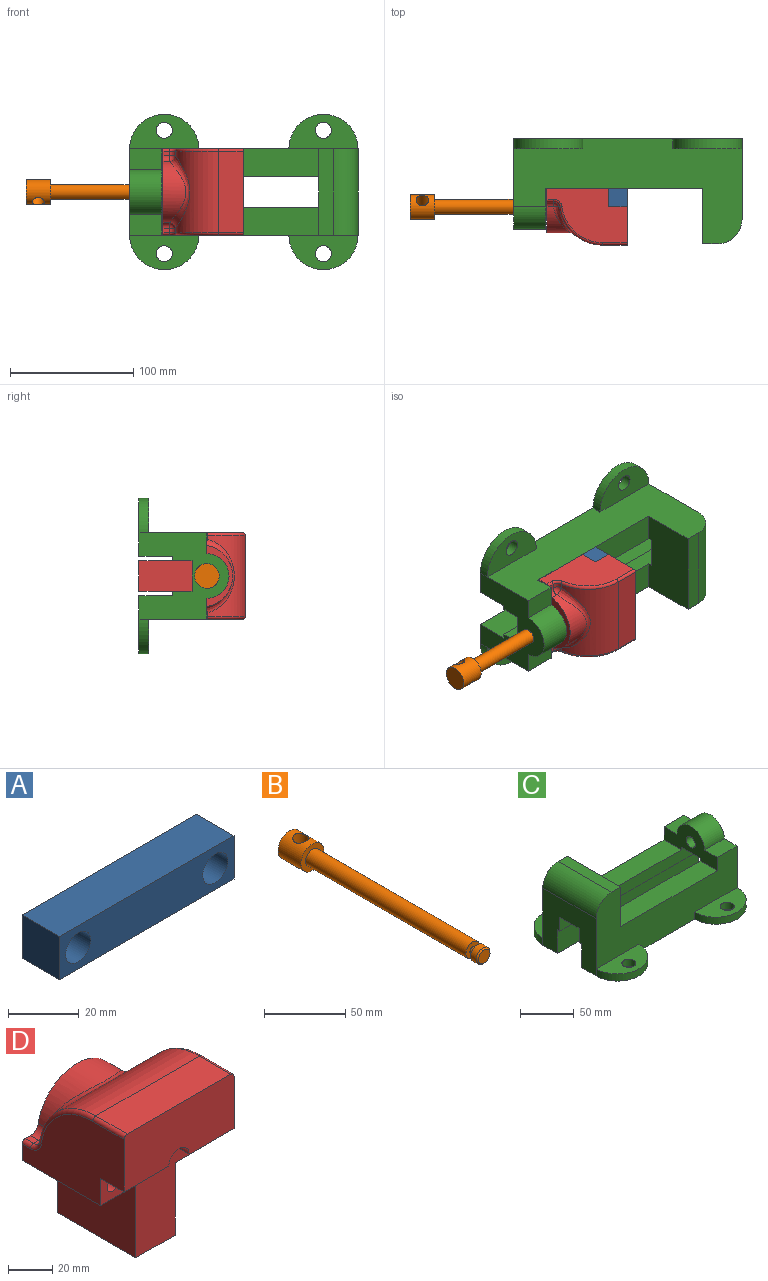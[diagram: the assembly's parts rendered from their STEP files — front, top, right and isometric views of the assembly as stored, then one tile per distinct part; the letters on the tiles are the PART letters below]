
ASSEMBLY  parts=4 mates=7
PART A: 16 faces, bbox 70x15x15 mm
  f0: plane 70x15mm, normal (0,1,0), area 958.9mm2, adj f1,f3,f4,f5,f6,f9,f12
  f1: plane 70x15mm, normal (0,0,1), area 1050mm2, adj f0,f2,f4,f5
  f2: plane 70x15mm, normal (0,-1,0), area 892.9mm2, adj f1,f3,f4,f5,f8,f11
  f3: plane 70x15mm, normal (0,0,-1), area 960mm2, adj f0,f2,f4,f5,f12,f13,f14,f15
  f4: plane 15x15mm, normal (1,0,0), area 225mm2, adj f0,f1,f2,f3
  f5: plane 15x15mm, normal (-1,0,0), area 225mm2, adj f0,f1,f2,f3
  f6: cylinder r=3.5mm len=7mm, axis (0,-1,0), area 110mm2, adj f0,f7
  f7: plane 10x10mm, normal (0,-1,0), area 40.1mm2, adj f6,f8
  f8: cylinder r=5mm len=10mm, axis (0,-1,0), area 314.2mm2, adj f2,f7
  f9: cylinder r=3.5mm len=7mm, axis (0,-1,0), area 110mm2, adj f0,f10
  f10: plane 10x10mm, normal (0,-1,0), area 40.1mm2, adj f9,f11
  f11: cylinder r=5mm len=10mm, axis (0,-1,0), area 314.2mm2, adj f2,f10
  f12: cylinder r=3mm len=6mm, axis (0,-1,0), area 28.3mm2, adj f0,f3,f13
  f13: plane 12x6mm, normal (0,-1,0), area 42.4mm2, adj f3,f12,f14
  f14: cylinder r=6mm len=12mm, axis (0,-1,0), area 113.1mm2, adj f3,f13,f15
  f15: plane 12x6mm, normal (0,1,0), area 56.5mm2, adj f3,f14
PART B: 11 faces, bbox 20x170x20 mm
  f0: plane 20x20mm, normal (0,1,0), area 314.2mm2, adj f1
  f1: cylinder r=10mm len=20mm, axis (0,1,0), area 1094.4mm2, adj f0,f2,f10
  f2: plane 20x20mm, normal (0,-1,0), area 201.1mm2, adj f1,f3
  f3: cylinder r=6mm len=140mm, axis (0,1,0), area 5277.9mm2, adj f2,f4
  f4: plane 12x12mm, normal (0,-1,0), area 93.5mm2, adj f3,f5
  f5: cylinder r=2.5mm len=5mm, axis (0,1,0), area 62.8mm2, adj f4,f6
  f6: plane 12x12mm, normal (0,1,0), area 93.5mm2, adj f5,f7
  f7: cylinder r=6mm len=12mm, axis (0,1,0), area 188.5mm2, adj f6,f9
  f8: plane 10x10mm, normal (0,-1,0), area 78.5mm2, adj f9
  f9: cone r=6mm half-angle=45deg, axis (0,1,0), area 48.9mm2, adj f7,f8
  f10: cylinder r=5mm len=20mm, axis (0,0,1), area 587mm2, adj f1
PART C: 36 faces, bbox 185x126x85 mm
  f0: plane 185x85mm, normal (0,1,0), area 8248.2mm2, adj f2,f3,f5,f6,f7,f8,f9,f10
  f1: plane 185x47mm, normal (0,0,-1), area 5712.5mm2, adj f2,f3,f11,f15,f30,f32,f33,f35
  f2: plane 73x70mm, normal (1,0,0), area 2981.8mm2, adj f0,f1,f9,f11,f12,f13,f14,f15
  f3: plane 70x65mm, normal (-1,0,0), area 3286mm2, adj f0,f1,f8,f9,f11,f15,f16,f17
  f4: plane 127x22.5mm, normal (0,0,1), area 2857.5mm2, adj f5,f6,f11,f22
  f5: plane 70x33mm, normal (-1,0,0), area 1370.8mm2, adj f0,f4,f10,f11,f12,f13,f14,f18
  f6: plane 70x45mm, normal (1,0,0), area 3075mm2, adj f0,f4,f7,f10,f11,f19,f21,f22
  f7: plane 70x12mm, normal (0,0,1), area 840mm2, adj f0,f6,f8,f11
  f8: cylinder r=20mm len=70mm, axis (0,1,0), area 2199.1mm2, adj f0,f3,f7,f11
  f9: plane 185x47mm, normal (0,0,-1), area 5712.5mm2, adj f0,f2,f3,f16,f25,f26,f28,f29
  f10: plane 127x22.5mm, normal (0,0,1), area 2857.5mm2, adj f0,f5,f6,f21
  f11: plane 185x85mm, normal (0,-1,0), area 8248.2mm2, adj f1,f2,f3,f4,f5,f6,f7,f8
  f12: cylinder r=18mm len=36mm, axis (1,0,0), area 1470.3mm2, adj f2,f5,f13,f14
  f13: plane 26x17mm, normal (0,0,1), area 442mm2, adj f2,f5,f11,f12
  f14: plane 26x17mm, normal (0,0,1), area 442mm2, adj f0,f2,f5,f12
  f15: plane 185x27mm, normal (0,1,0), area 4995mm2, adj f1,f2,f3,f20
  f16: plane 185x27mm, normal (0,-1,0), area 4995mm2, adj f2,f3,f9,f17
  f17: plane 185x3.5mm, normal (0,0,-1), area 647.5mm2, adj f2,f3,f16,f21
  f18: plane 26x25mm, normal (0,0,-1), area 650mm2, adj f2,f5,f21,f22
  f19: plane 32x25mm, normal (0,0,-1), area 800mm2, adj f3,f6,f21,f22
  f20: plane 185x3.5mm, normal (0,0,-1), area 647.5mm2, adj f2,f3,f15,f22
  f21: plane 185x16mm, normal (0,-1,0), area 2579mm2, adj f2,f3,f5,f6,f10,f17,f18,f19
  f22: plane 185x16mm, normal (0,1,0), area 2579mm2, adj f2,f3,f4,f5,f6,f18,f19,f20
  f23: cylinder r=6mm len=26mm, axis (1,0,0), area 980.2mm2, adj f2,f5
  f24: plane 56x28mm, normal (0,0,1), area 1098.8mm2, adj f0,f25,f26
  f25: cylinder r=28mm len=56mm, axis (0,0,-1), area 703.7mm2, adj f0,f2,f9,f24
  f26: cylinder r=6.5mm len=13mm, axis (0,0,-1), area 326.7mm2, adj f9,f24
  f27: plane 56x28mm, normal (0,0,1), area 1098.8mm2, adj f0,f28,f29
  f28: cylinder r=28mm len=56mm, axis (0,0,-1), area 703.7mm2, adj f0,f3,f9,f27
  f29: cylinder r=6.5mm len=13mm, axis (0,0,-1), area 326.7mm2, adj f9,f27
  f30: cylinder r=28mm len=56mm, axis (0,0,-1), area 703.7mm2, adj f1,f2,f11,f31
  f31: plane 56x28mm, normal (0,0,1), area 1098.8mm2, adj f11,f30,f32
  f32: cylinder r=6.5mm len=13mm, axis (0,0,-1), area 326.7mm2, adj f1,f31
  f33: cylinder r=28mm len=56mm, axis (0,0,-1), area 703.7mm2, adj f1,f3,f11,f34
  f34: plane 56x28mm, normal (0,0,1), area 1098.8mm2, adj f11,f33,f35
  f35: cylinder r=6.5mm len=13mm, axis (0,0,-1), area 326.7mm2, adj f1,f34
PART D: 35 faces, bbox 70x65x88.9 mm
  f0: plane 28.5x15mm, normal (0,0,-1), area 427.5mm2, adj f6,f7,f9,f17
  f1: plane 28.5x15mm, normal (0,0,-1), area 427.5mm2, adj f6,f8,f9,f17
  f2: plane 5.31x3.42mm, normal (0,0,1), area 18.2mm2, adj f5,f20,f21,f34
  f3: cylinder r=35mm len=66mm, axis (-1,0,0), area 2250.4mm2, adj f11,f21,f22,f26,f28,f32
  f4: plane 50x25mm, normal (0,0,-1), area 1250mm2, adj f5,f6,f12,f14
  f5: plane 76x70mm, normal (0,1,0), area 2557mm2, adj f2,f4,f7,f8,f10,f12,f13,f14
  f6: plane 70x55mm, normal (0,-1,0), area 1915.2mm2, adj f0,f1,f4,f7,f8,f12,f13,f14
  f7: plane 65x44mm, normal (1,0,0), area 1990.2mm2, adj f0,f5,f6,f9,f15,f31,f32,f33
  f8: plane 65x44mm, normal (-1,0,0), area 1990.2mm2, adj f1,f5,f6,f9,f13,f27,f28,f29
  f9: plane 70x31mm, normal (0,-1,0), area 2101.9mm2, adj f0,f1,f7,f8,f11,f17,f27,f31
  f10: plane 5.31x3.42mm, normal (0,0,1), area 18.2mm2, adj f5,f22,f23,f30
  f11: plane 66x20mm, normal (0,0,1), area 1320mm2, adj f3,f9,f27,f31
  f12: plane 50x40mm, normal (-1,0,0), area 2000mm2, adj f4,f5,f6,f13
  f13: plane 50x22.5mm, normal (0,0,-1), area 1125mm2, adj f5,f6,f8,f12
  f14: plane 50x40mm, normal (1,0,0), area 2000mm2, adj f4,f5,f6,f15
  f15: plane 50x22.5mm, normal (0,0,-1), area 1125mm2, adj f5,f6,f7,f14
  f16: cylinder r=25mm len=49.3mm, axis (0,1,0), area 854.7mm2, adj f5,f20,f23,f26
  f17: cylinder r=6.5mm len=65mm, axis (0,1,0), area 2348.3mm2, adj f0,f1,f5,f6,f9
  f18: cylinder r=3.3mm len=50mm, axis (0,1,0), area 1036.7mm2, adj f5,f6
  f19: cylinder r=3.3mm len=50mm, axis (0,1,0), area 1036.7mm2, adj f5,f6
  f20: cylinder r=5mm len=5.31mm, axis (0,1,0), area 37.3mm2, adj f2,f5,f16,f24
  f21: cylinder r=5mm len=4.96mm, axis (-1,0,0), area 24.7mm2, adj f2,f3,f24,f33
  f22: cylinder r=5mm len=4.96mm, axis (-1,0,0), area 24.7mm2, adj f3,f10,f25,f29
  f23: cylinder r=5mm len=5.31mm, axis (0,1,0), area 37.3mm2, adj f5,f10,f16,f25
  f24: sphere r=5mm, area 32mm2, adj f20,f21,f26
  f25: sphere r=5mm, area 32mm2, adj f22,f23,f26
  f26: bspline ~59.69x24.08mm, area 433.7mm2, adj f3,f16,f24,f25
  f27: cylinder r=2mm len=20mm, axis (0,-1,0), area 62.8mm2, adj f8,f9,f11,f28
  f28: torus R=33mm, axis (1,0,0), area 155.6mm2, adj f3,f8,f27,f29
  f29: torus R=7mm, axis (1,0,0), area 26mm2, adj f8,f22,f28,f30
  f30: cylinder r=2mm len=5.31mm, axis (0,-1,0), area 16.7mm2, adj f5,f8,f10,f29
  f31: cylinder r=2mm len=20mm, axis (0,1,0), area 62.8mm2, adj f7,f9,f11,f32
  f32: torus R=33mm, axis (1,0,0), area 155.6mm2, adj f3,f7,f31,f33
  f33: torus R=7mm, axis (1,0,0), area 26mm2, adj f7,f21,f32,f34
  f34: cylinder r=2mm len=5.31mm, axis (0,1,0), area 16.7mm2, adj f2,f5,f7,f33
PLACE A rot(axis=(-0.58,0.58,0.58),120deg) t=(-8.06,-47.5,-16)mm
PLACE B rot(axis=(0.69,-0.69,0.21),156.2deg) t=(-47.65,-55,-16)mm
PLACE C rot(axis=(0,-0.71,0.71),180deg) t=(0,-42.5,-16)mm
PLACE D rot(axis=(0.58,-0.58,0.58),120deg) t=(-34.43,-32.42,-16)mm
MATE cylindrical B.f1 <-> C.f23  axis (-1,0,0) through (-86.56,-55,-16)mm
MATE planar A.f4 <-> D.f8  axis (0,0,-1) through (-8.06,-47.5,-51)mm
MATE planar B.f1 <-> A.f13  axis (-1,0,0) through (-12.56,-55,-16)mm
MATE planar D.f15 <-> C.f4  axis (0,1,0) through (-40.56,-40,7.75)mm
MATE planar A.f0 <-> D.f6  axis (-1,0,0) through (-15.56,-47.41,-16)mm
MATE planar A.f3 <-> D.f1  axis (0,-1,0) through (-6.56,-55,-16)mm
MATE planar D.f14 <-> C.f22  axis (0,0,1) through (-40.56,-20,-3.5)mm
